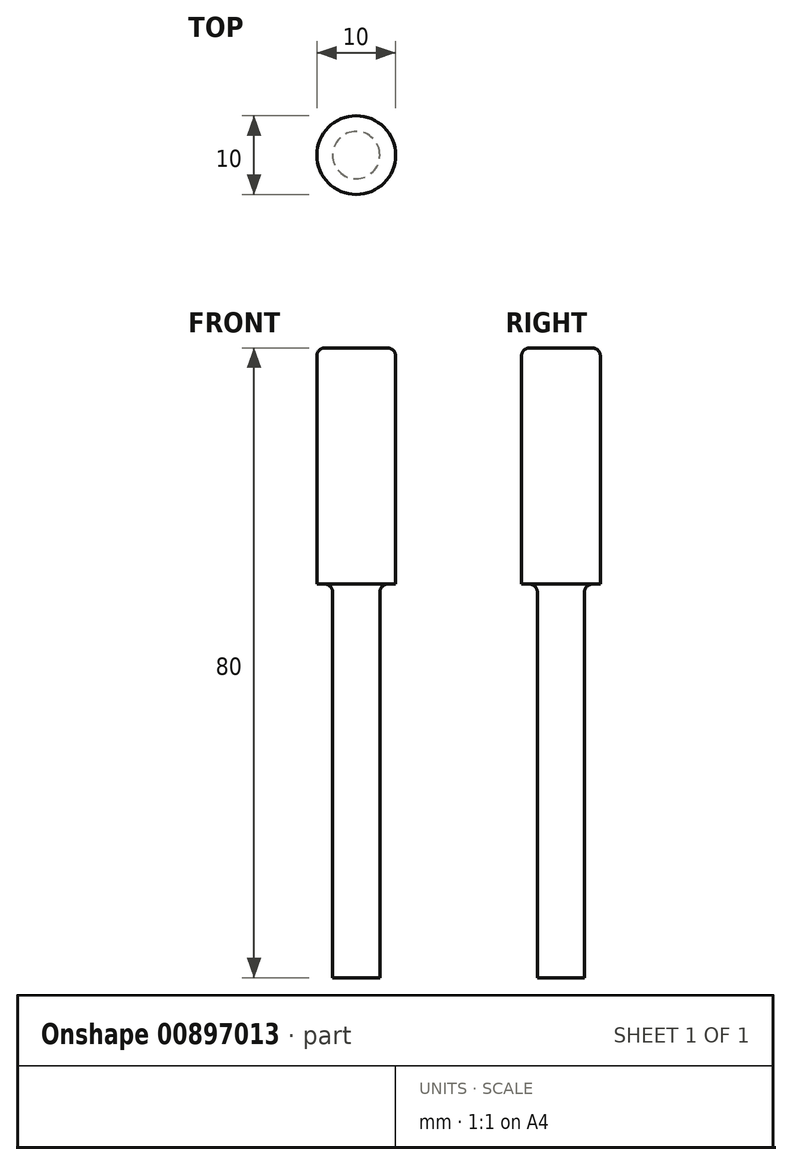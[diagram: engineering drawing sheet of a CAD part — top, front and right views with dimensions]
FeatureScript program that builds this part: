
annotation { "Feature Type Name" : "Feature", "Feature Type Description" : "" }
export const myFeature = defineFeature(function(context is Context, id is Id, definition is map)
    precondition{}
    {
        {
            var Q0;
            Q0=qCreatedBy(makeId("Front.planeOp"),FACE);
            var sketch = newSketch(context, id + "F0", { "sketchPlane" : qUnion([Q0])});
            skLineSegment(sketch, "E0", {"start": v(0, 0) * mm, "end": v(0, 80) * mm});
            skLineSegment(sketch, "E1", {"start": v(0, 80) * mm, "end": v(4, 80) * mm});
            skLineSegment(sketch, "E2", {"start": v(5, 79) * mm, "end": v(5, 50) * mm});
            skLineSegment(sketch, "E3", {"start": v(5, 50) * mm, "end": v(4, 50) * mm});
            skLineSegment(sketch, "E4", {"start": v(3, 49) * mm, "end": v(3, 0) * mm});
            skLineSegment(sketch, "E5", {"start": v(3, 0) * mm, "end": v(0, 0) * mm});
            skPoint(sketch, "E6.visualSharp", {"position": v(5, 80) * mm});
            skArc(sketch, "E6.filletArc", {"start": v(5, 79) * mm, "mid": v(4.7, 79.7) * mm, "end": v(4, 80) * mm});
            skPoint(sketch, "E7.visualSharp", {"position": v(3, 50) * mm});
            skArc(sketch, "E7.filletArc", {"start": v(4, 50) * mm, "mid": v(3.3, 49.7) * mm, "end": v(3, 49) * mm});
            skSolve(sketch);
        }
        {
            var Q0;
            Q0=makeQuery(id+"F0.imprint","IMPRINT",FACE,{"disambiguationData":[TD([[makeQuery(id+"F0.imprint","IMPRINT",EDGE,{"derivedFrom":sQuery(id+"F0.wireOp",EDGE,"E0")}),-1.0]])]});
            var Q1;
            Q1=sQuery(id+"F0.wireOp",EDGE,"E0");
            revolve(context, id + "F1", {"surfaceOperationType" : NewSurfaceOperationType.NEW, "entities" : qUnion([Q0]), "axis" : qUnion([Q1]), "revolveType" : RevolveType.FULL});
        }
    });
